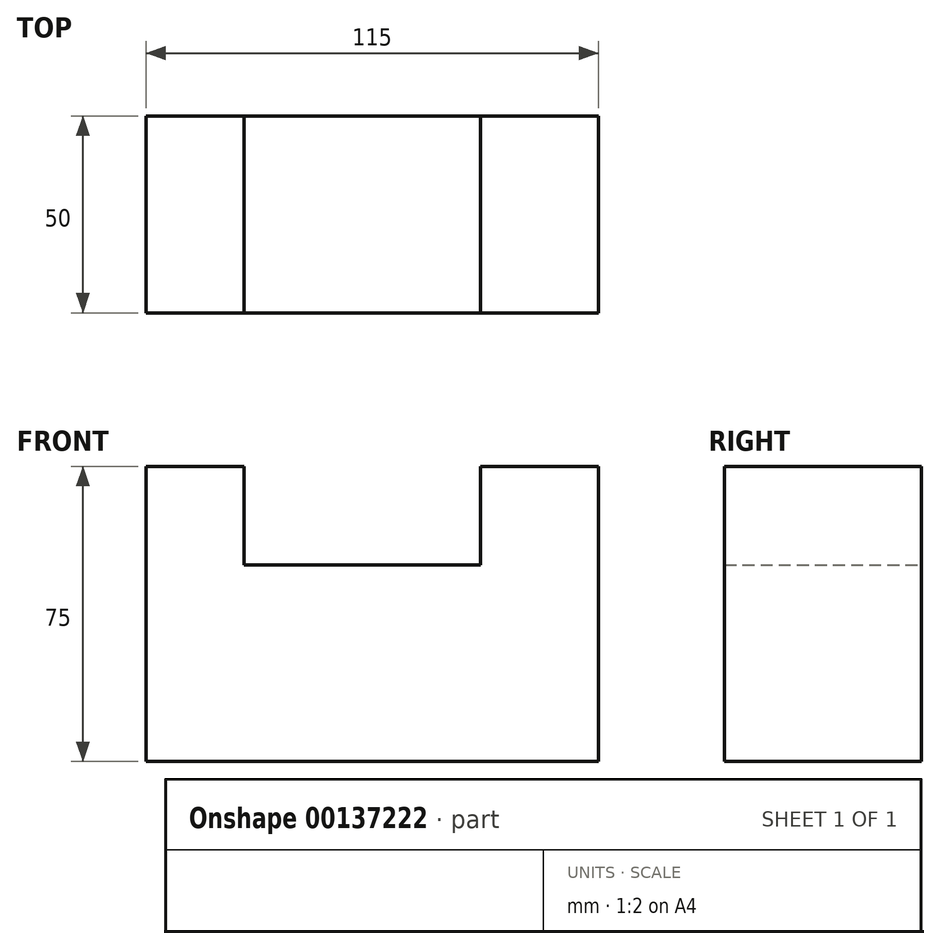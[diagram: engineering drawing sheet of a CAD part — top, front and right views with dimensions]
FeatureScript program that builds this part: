
annotation { "Feature Type Name" : "Feature", "Feature Type Description" : "" }
export const myFeature = defineFeature(function(context is Context, id is Id, definition is map)
    precondition{}
    {
        {
            var Q0;
            Q0=qCreatedBy(makeId("Front.planeOp"),FACE);
            var sketch = newSketch(context, id + "F0", { "sketchPlane" : qUnion([Q0])});
            skLineSegment(sketch, "E0", {"start": v(0, 0) * mm, "end": v(0, 75) * mm});
            skLineSegment(sketch, "E1", {"start": v(0, 75) * mm, "end": v(25, 75) * mm});
            skLineSegment(sketch, "E2", {"start": v(25, 75) * mm, "end": v(25, 50) * mm});
            skLineSegment(sketch, "E3", {"start": v(25, 50) * mm, "end": v(85, 50) * mm});
            skLineSegment(sketch, "E4", {"start": v(85, 50) * mm, "end": v(85, 75) * mm});
            skLineSegment(sketch, "E5", {"start": v(85, 75) * mm, "end": v(115, 75) * mm});
            skLineSegment(sketch, "E6", {"start": v(115, 75) * mm, "end": v(115, 0) * mm});
            skLineSegment(sketch, "E7", {"start": v(115, 0) * mm, "end": v(0, 0) * mm});
            skSolve(sketch);
        }
        {
            var Q0;
            Q0 = qSketchRegion(id + "F0", true);
            extrude(context, id + "F1", {"entities" : qUnion([Q0]), "depth" : 50 * mm});
        }
    });
